# Revit family: Time Max K
name_source: partatom
category: Attrezzatura meccanica
units: mm (PartAtom-declared; Revit-internal decimal feet)

## family parameters
Basato su piano di lavoro = No
Classificazione = Nessuno
Condiviso = No
Mantieni orientamento annotazione = No
Punto di calcolo locali = No
Quota connettore circolare = Usa diametro
Sempre verticale = Sì
Taglio con vuoti quando caricato = No
Tipo di parte = Normale

## types (2) — shared parameters
Combustion air inlet - separate system = 80 mm  [stored 0.262467 ft]
Date of publishing = 15/02/2024
Depth = 425 mm  [stored 1.39436 ft]
Design country = Italy
Domestic Cold Water Diameter = 21 mm  [stored 0.0688976 ft]
Domestic Hot Water Diameter = 21 mm  [stored 0.0688976 ft]
Flue outlet = 100 mm  [stored 0.328084 ft]
Gas Inlet Diameter = 26 mm
Height = 900 mm  [stored 2.95276 ft]
Hydronic Return Diameter = 26 mm
Hydronic Supply Diameter = 26 mm
IFC Classification = Boiler
Manufacturer country = Italy
Manufacturer name = Italtherm S.p.A.
Material main = Metal
Material secondary = Plastic
NBS reference Description = Boiler
Omniclass Description = Condensing boilers
Power consumption (W) = 100 W
Power supply | Frequency (Hz) = 50 Hz
Power supply | Phase = 1
Power supply | Voltage (V) = 230 V
Product family = Heating
Product group = Thermal unit
Siphon with condensate drain = 25 mm  [stored 0.082021 ft]
Uniclass 2015 Name = Boiler
Width = 600 mm  [stored 1.9685 ft]
zero-valued in all types: Prospetto di default

## per-type parameters (varying)
| type | Efficiency 30% | Maximum heat output 50/30°C | Maximum heat output 80/60°C | Maximum heating heat input | Minimum heat output 50/30°C | Minimum heat output 80/60°C | Nominal efficiency 50/30°C | Nominal efficiency 80/60°C | Weight |
| Time Max 27 K | 107,60% | 27200 W | 25100 W | 26000 W | 2700 W | 2500 W | 104,70% | 96,60% | 61,50 kg |
| Time Max 35 K | 0,00% | 34700 W | 32000 W | 33000 W | 3600 W | 3200 W | 105,10% | 97,00% | 63,50 kg |

note: [stored X ft] marks values corroborated as IEEE doubles in the binary element streams (Revit-internal decimal feet)
